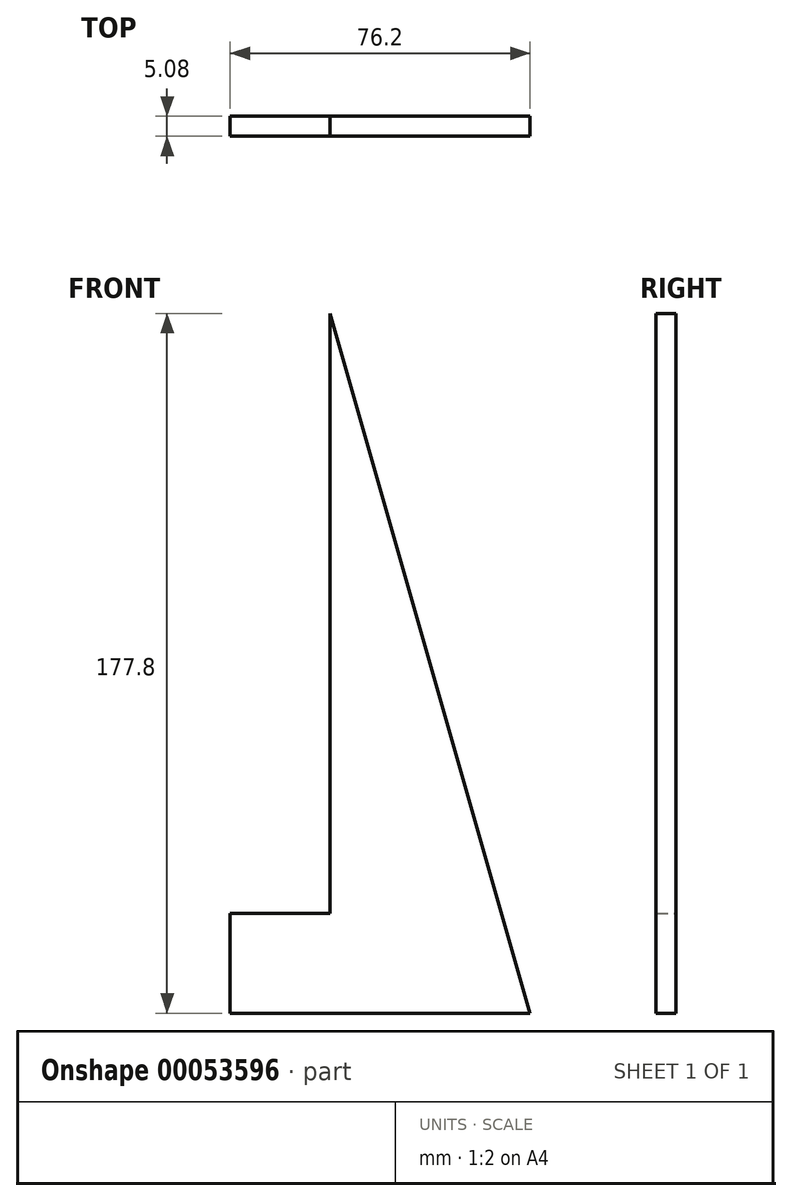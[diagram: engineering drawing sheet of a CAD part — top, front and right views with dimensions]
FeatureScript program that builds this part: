
annotation { "Feature Type Name" : "Feature", "Feature Type Description" : "" }
export const myFeature = defineFeature(function(context is Context, id is Id, definition is map)
    precondition{}
    {
        {
            var Q0;
            Q0=qCreatedBy(makeId("Front.planeOp"),FACE);
            var sketch = newSketch(context, id + "F0", { "sketchPlane" : qUnion([Q0])});
            skLineSegment(sketch, "E0.top", {"start": v(0, 25.4) * mm, "end": v(-25.4, 25.4) * mm});
            skLineSegment(sketch, "E0.right", {"start": v(-25.4, 0) * mm, "end": v(-25.4, 25.4) * mm});
            skLineSegment(sketch, "E1", {"start": v(0, 25.4) * mm, "end": v(0, 177.8) * mm});
            skLineSegment(sketch, "E2", {"start": v(-25.4, 0) * mm, "end": v(50.8, 0) * mm});
            skLineSegment(sketch, "E3", {"start": v(50.8, 0) * mm, "end": v(0, 177.8) * mm});
            skSolve(sketch);
        }
        {
            var Q0;
            Q0=makeQuery(id+"F0.imprint","IMPRINT",FACE,{"disambiguationData":[TD([[makeQuery(id+"F0.imprint","IMPRINT",EDGE,{"derivedFrom":sQuery(id+"F0.wireOp",EDGE,"6PGGvJm2-WKcb-B5lW-wTXe-0cnfVu7FarSk")}),1.0]])]});
            var Q1;
            Q1=makeQuery(id+"F0.imprint","IMPRINT",FACE,{"disambiguationData":[TD([[makeQuery(id+"F0.imprint","IMPRINT",EDGE,{"derivedFrom":sQuery(id+"F0.wireOp",EDGE,"E0.bottom")}),-1.0]])]});
            var Q2;
            Q2=makeQuery(id+"F0.imprint","IMPRINT",FACE,{"disambiguationData":[TD([[makeQuery(id+"F0.imprint","IMPRINT",EDGE,{"derivedFrom":sQuery(id+"F0.wireOp",EDGE,"E0.top")}),1.0]])]});
            extrude(context, id + "F1", {"entities" : qUnion([Q0, Q1, Q2]), "depth" : 5.08 * mm});
        }
    });
